# Revit family: sfera_d50
name_source: partatom
category: Антураж
revit_build: Autodesk Revit 2017 (Build: 20160225_1515(x64)
units: mm (PartAtom-declared; Revit-internal decimal feet)

## family parameters
Всегда вертикально = Да
Источник визуального образа = Геометрия семейства
На основе рабочей плоскости = Нет
Общий = Нет
При загрузке вырезать с полостями = Нет
Точка расчета площади = Нет

## types (6) — shared parameters
Диаметр = 500 мм
Наименование = Сфера "D50"
Объем бетона = 0.06 м³
Производитель = ГК Очаковский комбинат ЖБИ
zero-valued in all types: Высота

## per-type parameters (varying)
| type | URL | Материал |
| "D50" Белый шелк |  | Очаковский_Белый_Шелк |
| "D50" Крымский берег | http://file-system.ru | Очаковский_Крымский_берег |
| "D50" Морская соль |  | Очаковский_Морская_соль |
| "D50" Московский гравий |  | Очаковский_Московский_гравий |
| "D50" Черный шелк |  | Очаковский_Черный_шелк |
| "D50" Шахматка |  | Очаковский_Шахматка |

## geometry (parser evidence)
native form markers: Blend x159
no freeform markers — native parametric forms only
